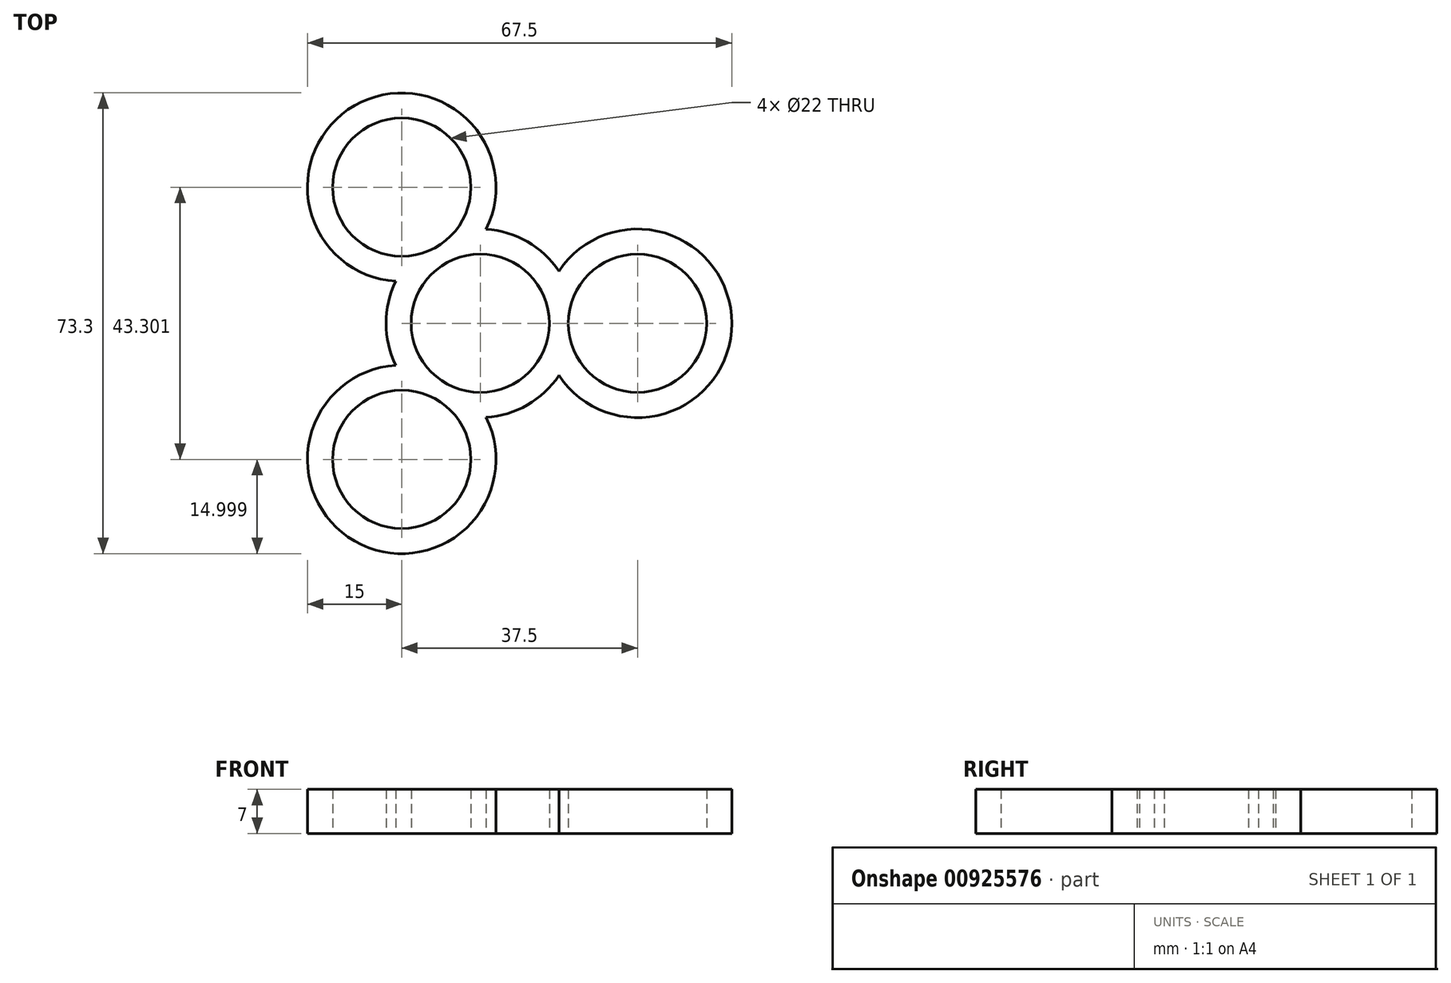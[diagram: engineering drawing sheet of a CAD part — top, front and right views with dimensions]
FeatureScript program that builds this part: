
annotation { "Feature Type Name" : "Feature", "Feature Type Description" : "" }
export const myFeature = defineFeature(function(context is Context, id is Id, definition is map)
    precondition{}
    {
        {
            var Q0;
            Q0=qCreatedBy(makeId("Top.planeOp"),FACE);
            var sketch = newSketch(context, id + "F0", { "sketchPlane" : qUnion([Q0])});
            skArc(sketch, "E0", {"start": v(5.5, -9.53) * mm, "mid": v(11, 0) * mm, "end": v(5.5, 9.53) * mm});
            skCircle(sketch, "E1", {"center": v(25, 0) * mm, "radius": 11 * mm});
            skArc(sketch, "E2", {"start": v(12.5, -8.3) * mm, "mid": v(40, 0) * mm, "end": v(12.5, 8.3) * mm});
            skArc(sketch, "E3", {"start": v(12.5, 8.3) * mm, "mid": v(10.27, 10.93) * mm, "end": v(7.5, 13) * mm});
            skArc(sketch, "E4.trimOffspring", {"start": v(7.5, -13) * mm, "mid": v(10.27, -10.93) * mm, "end": v(12.5, -8.3) * mm});
            skArc(sketch, "E5.1.0", {"start": v(0.93, 14.97) * mm, "mid": v(-20, 34.64) * mm, "end": v(-13.43, 6.68) * mm});
            skCircle(sketch, "E5.1.1", {"center": v(-12.5, 21.65) * mm, "radius": 11 * mm});
            skArc(sketch, "E5.1.2", {"start": v(-13.43, 6.68) * mm, "mid": v(-14.6, 3.43) * mm, "end": v(-15, 0) * mm});
            skArc(sketch, "E5.1.3", {"start": v(5.5, 9.53) * mm, "mid": v(-5.5, 9.53) * mm, "end": v(-11, 0) * mm});
            skArc(sketch, "E5.1.4", {"start": v(7.5, 13) * mm, "mid": v(4.33, 14.36) * mm, "end": v(0.93, 14.97) * mm});
            skArc(sketch, "E5.2.0", {"start": v(-13.43, -6.68) * mm, "mid": v(-20, -34.64) * mm, "end": v(0.93, -14.97) * mm});
            skCircle(sketch, "E5.2.1", {"center": v(-12.5, -21.65) * mm, "radius": 11 * mm});
            skArc(sketch, "E5.2.2", {"start": v(0.93, -14.97) * mm, "mid": v(4.33, -14.36) * mm, "end": v(7.5, -13) * mm});
            skArc(sketch, "E5.2.3", {"start": v(-11, 0) * mm, "mid": v(-5.5, -9.53) * mm, "end": v(5.5, -9.53) * mm});
            skArc(sketch, "E5.2.4", {"start": v(-15, 0) * mm, "mid": v(-14.6, -3.43) * mm, "end": v(-13.43, -6.68) * mm});
            skSolve(sketch);
        }
        {
            var Q0;
            Q0 = qSketchRegion(id + "F0", true);
            extrude(context, id + "F1", {"entities" : qUnion([Q0]), "depth" : 7 * mm, "offsetDistance" : 25 * mm});
        }
    });
